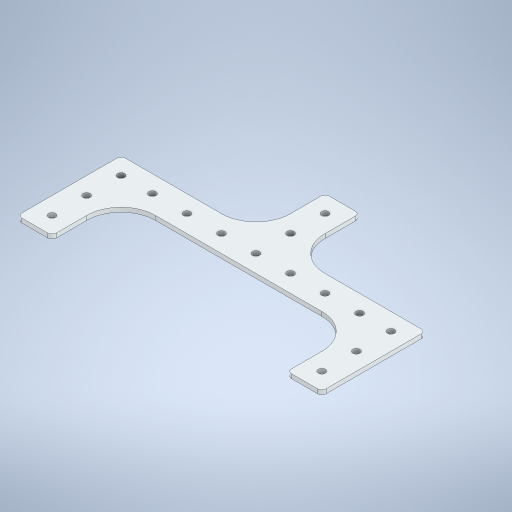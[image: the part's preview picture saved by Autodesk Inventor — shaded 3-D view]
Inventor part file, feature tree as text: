
AUTODESK INVENTOR PART (.ipt)
format: ipt  version: 2024 (Build 280153000, 153)  size: 399,872 bytes
history: native  units: in
note: dims shown in document units (in); Inventor stores cm internally (conversion verified against a paired STEP export)
features: extrude x5, sketch x4, fillet x4
ambient origin geometry x8: Origin, YZ Plane, XZ Plane, XY Plane, X Axis, Y Axis, Z Axis, Center Point
bodies: Solid1 (feature_tree)
feature tree (13):
  sketch  "Sketch1"  dims[d0=1.9055in d1=1.9055in]
  extrude  "Extrusion1"  Depth=1.9055in
  extrude  "Extrusion2"  Depth=0.125in TaperAngle=0.0deg
  extrude  "Extrusion3"  Depth=1.0in
  fillet  "Fillet1"  Radius=0.201in
  extrude  "Extrusion4"  Depth=1.0in
  extrude  "Extrusion5"  Depth=1.0in
  fillet  "Fillet3"  Radius=0.201in
  fillet  "Fillet4"  Radius=0.201in
  sketch  "Sketch2"  dims[d2=0.125in d3=0.0in d4=0.125in d5=0.0in]
  sketch  "Sketch4"  dims[d6=1.0in d8=0.5in d9=0.201in]
  sketch  "Sketch5"  dims[d10=0.201in d11=1.0in d12=0.5in d13=0.201in d14=0.201in d15=0.375in d16=0.0in d17=0.125in d23=1.0in d24=3.0in d25=1.0in d26=0.125in d27=0.0in d28=1.0in d29=1.0in d30=1.0in d31=1.0in d32=0.201in d33=0.201in d34=0.201in d35=0.201in d36=0.25in d37=0.0in d38=0.125in d39=1.0in]
  fillet  "Fillet2"  Radius=0.375in
